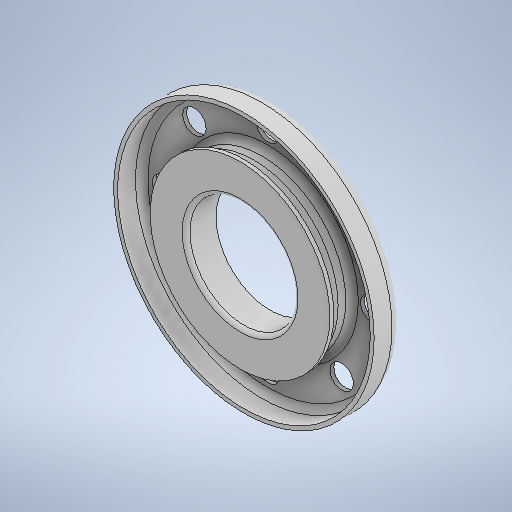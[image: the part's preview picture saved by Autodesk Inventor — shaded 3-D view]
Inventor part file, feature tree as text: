
AUTODESK INVENTOR PART (.ipt)
format: ipt  version: 2025 (Build 290162010, 162A)  size: 411,136 bytes
history: native  units: mm
features: other x12, sketch x3, revolve x2, extrude x1, pattern_circular x1
ambient origin geometry x8: Origin, YZ Plane, XZ Plane, XY Plane, X Axis, Y Axis, Z Axis, Center Point
bodies: Solid1 (feature_tree)
feature tree (19):
  other  "Table"
  other  "Stamp flange DIN2642-015"
  other  "Stamp flange DIN2642-020"
  other  "Stamp flange DIN2642-025"
  other  "Stamp flange DIN2642-032"
  other  "Stamp flange DIN2642-040"
  other  "Stamp flange DIN2642-050"
  other  "Stamp flange DIN2642-065"
  other  "Stamp flange DIN2642-080"
  other  "Stamp flange DIN2642-100"
  other  "Stamp flange DIN2642-125"
  other  "Stamp flange DIN2642-150"
  revolve  "Revolution1"  [1 undecoded]
  revolve  "Revolution2"  Angle=90.0deg
  extrude  "Extrusion1"  TaperAngle=360.0deg  [1 undecoded]
  pattern_circular  "Circular Pattern1"  [2 undecoded]
  sketch  "Sketch1"  dims[d7=90.0deg d8=3.0mm]
  sketch  "Sketch2"  dims[d10=4.8125mm d15=90.0deg]
  sketch  "Sketch3"  dims[d18=0.0mm d19=0.0mm d21=360.0deg d23=38.5mm d26=3.0mm]
note: 4 required parameter values undecoded (feature->parameter linkage not recoverable at this tier; creation-order binding heuristic only, values carry confidence <= 0.55)